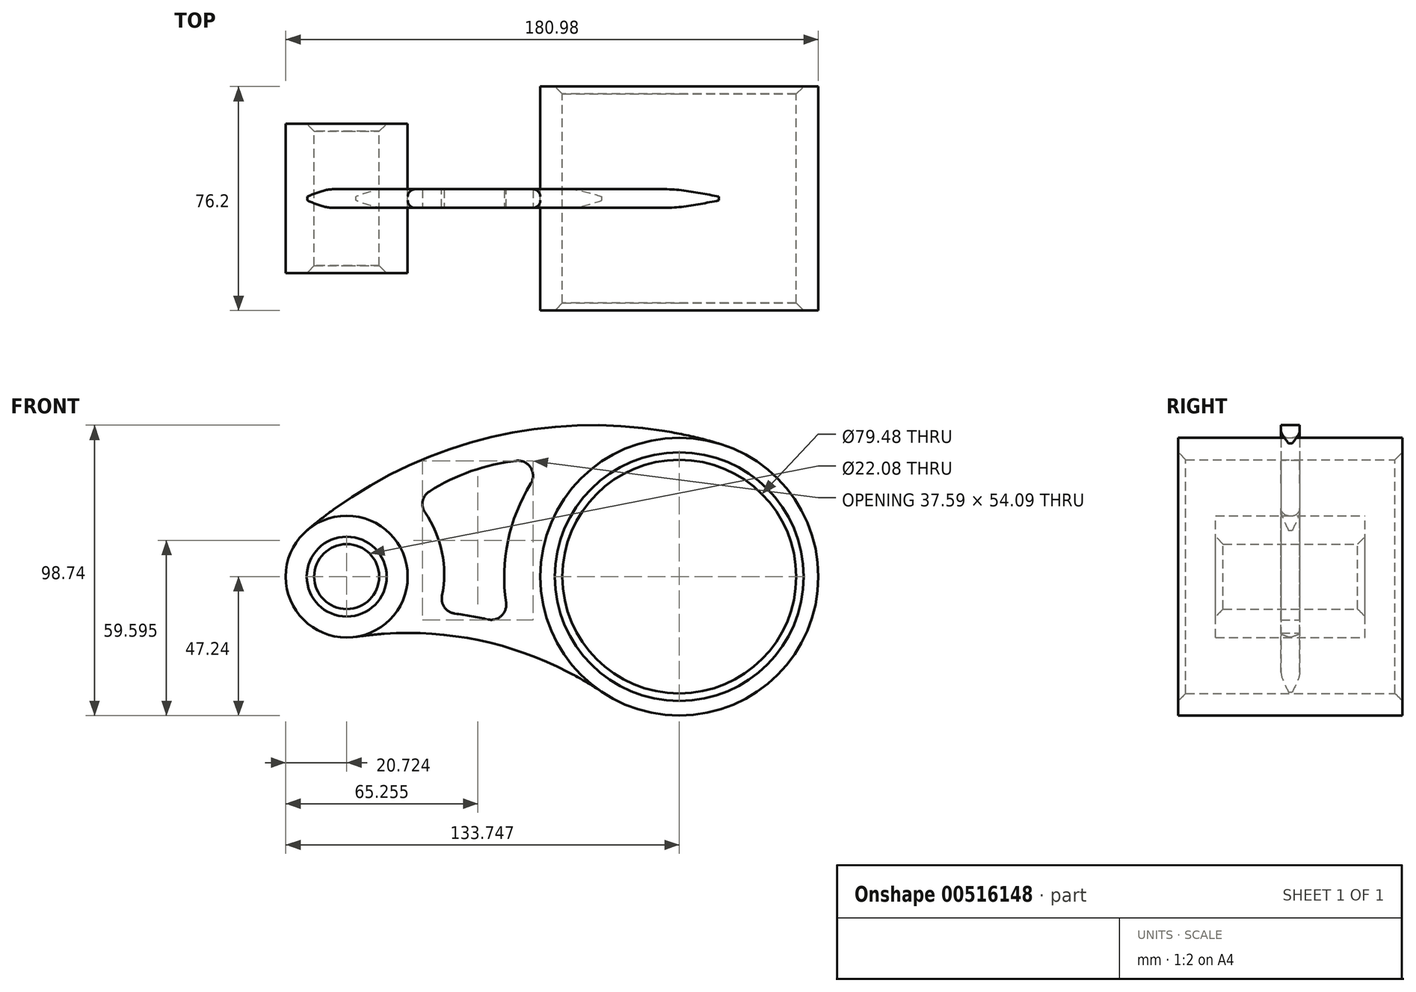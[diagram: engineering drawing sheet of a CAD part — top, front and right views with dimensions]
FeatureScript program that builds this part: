
annotation { "Feature Type Name" : "Feature", "Feature Type Description" : "" }
export const myFeature = defineFeature(function(context is Context, id is Id, definition is map)
    precondition{}
    {
        {
            var Q0;
            Q0=qCreatedBy(makeId("Front.planeOp"),FACE);
            var sketch = newSketch(context, id + "F0", { "sketchPlane" : qUnion([Q0])});
            skCircle(sketch, "E0", {"center": v(-66.18, 0) * mm, "radius": 11.04 * mm});
            skCircle(sketch, "E1", {"center": v(-66.18, 0) * mm, "radius": 20.73 * mm});
            skSolve(sketch);
        }
        {
            var Q0;
            Q0 = qSketchRegion(id + "F0", true);
            extrude(context, id + "F1", {"entities" : qUnion([Q0]), "endBound" : BoundingType.SYMMETRIC, "depth" : 50.8 * mm, "offsetDistance" : 25.4 * mm});
        }
        {
            var Q0;
            Q0=qCreatedBy(makeId("Front.planeOp"),FACE);
            var sketch = newSketch(context, id + "F2", { "sketchPlane" : qUnion([Q0])});
            skCircle(sketch, "E2", {"center": v(46.85, 0) * mm, "radius": 47.24 * mm});
            skCircle(sketch, "E3", {"center": v(46.85, 0) * mm, "radius": 39.74 * mm});
            skSolve(sketch);
        }
        {
            var Q0;
            Q0=makeQuery(id+"F2.imprint","IMPRINT",FACE,{"disambiguationData":[TD([[makeQuery(id+"F2.imprint","IMPRINT",EDGE,{"derivedFrom":sQuery(id+"F2.wireOp",EDGE,"E2")}),1.0]])]});
            extrude(context, id + "F3", {"entities" : qUnion([Q0]), "endBound" : BoundingType.SYMMETRIC, "depth" : 76.2 * mm, "offsetDistance" : 25.4 * mm});
        }
        {
            var Q0;
            Q0=qCreatedBy(makeId("Front.planeOp"),FACE);
            var sketch = newSketch(context, id + "F4", { "sketchPlane" : qUnion([Q0])});
            skArc(sketch, "E4.0", {"start": v(-63.08, -20.5) * mm, "mid": v(-47.31, 8.59) * mm, "end": v(-79.6, 15.8) * mm});
            skArc(sketch, "E5", {"start": v(60.31, 45.28) * mm, "mid": v(-13.38, 48.28) * mm, "end": v(-79.6, 15.8) * mm});
            skArc(sketch, "E6", {"start": v(20.53, -39.23) * mm, "mid": v(-19.52, -22.03) * mm, "end": v(-63.08, -20.5) * mm});
            skArc(sketch, "E7.0", {"start": v(60.31, 45.28) * mm, "mid": v(4.1, 20.12) * mm, "end": v(20.53, -39.23) * mm});
            skSolve(sketch);
        }
        {
            var Q0;
            Q0 = qSketchRegion(id + "F4", true);
            extrude(context, id + "F5", {"entities" : qUnion([Q0]), "endBound" : BoundingType.SYMMETRIC, "depth" : 6.35 * mm, "offsetDistance" : 25.4 * mm});
        }
        {
            var Q0;
            Q0=makeQuery(id+"F5.opExtrude","CAP_EDGE",EDGE,{"disambiguationData":[OSD([sQuery(id+"F4.wireOp",EDGE,"E4.0")])],"isStart":false});
            var Q1;
            Q1=makeQuery(id+"F5.opExtrude","CAP_EDGE",EDGE,{"disambiguationData":[OSD([sQuery(id+"F4.wireOp",EDGE,"E4.0")])],"isStart":true});
            var Q2;
            Q2=makeQuery(id+"F5.opExtrude","CAP_EDGE",EDGE,{"disambiguationData":[OSD([sQuery(id+"F4.wireOp",EDGE,"E7.0")])],"isStart":true});
            var Q3;
            Q3=makeQuery(id+"F5.opExtrude","CAP_EDGE",EDGE,{"disambiguationData":[OSD([sQuery(id+"F4.wireOp",EDGE,"E7.0")])],"isStart":false});
            var Q4;
            Q4=makeQuery(id+"F5.opExtrude","CAP_EDGE",EDGE,{"disambiguationData":[OSD([sQuery(id+"F4.wireOp",EDGE,"E7.0")])],"isStart":false});
            fillet(context, id + "F6", {"entities" : qUnion([Q0, Q1, Q2, Q3, Q4]), "radius" : 2.54 * mm, "tangentPropagation" : true, "allowEdgeOverflow" : false});
        }
        {
            var Q0;
            Q0=makeQuery(id+"F1.opExtrude","CAP_EDGE",EDGE,{"disambiguationData":[OSD([sQuery(id+"F0.wireOp",EDGE,"E0")])],"isStart":false});
            var Q1;
            Q1=makeQuery(id+"F3.opExtrude","CAP_EDGE",EDGE,{"disambiguationData":[OSD([sQuery(id+"F2.wireOp",EDGE,"E3")])],"isStart":false});
            var Q2;
            Q2=makeQuery(id+"F3.opExtrude","CAP_EDGE",EDGE,{"disambiguationData":[OSD([sQuery(id+"F2.wireOp",EDGE,"E3")])],"isStart":true});
            var Q3;
            Q3=makeQuery(id+"F1.opExtrude","CAP_EDGE",EDGE,{"disambiguationData":[OSD([sQuery(id+"F0.wireOp",EDGE,"E0")])],"isStart":true});
            chamfer(context, id + "F7", {"entities" : qUnion([Q0, Q1, Q2, Q3]), "width" : 2.54 * mm, "tangentPropagation" : true});
        }
        {
            var Q0;
            Q0=makeQuery(id+"F5.opExtrude","CAP_FACE",FACE,{"disambiguationData":[OSD([sQuery(id+"F4.wireOp",EDGE,"E4.0"),sQuery(id+"F4.wireOp",EDGE,"E5"),sQuery(id+"F4.wireOp",EDGE,"E6"),sQuery(id+"F4.wireOp",EDGE,"E7.0")])],"isStart":false});
            var sketch = newSketch(context, id + "F8", { "sketchPlane" : qUnion([Q0])});
            skArc(sketch, "E8", {"start": v(2.37, 39.8) * mm, "mid": v(-21.37, 36.7) * mm, "end": v(-42.7, 25.81) * mm});
            skArc(sketch, "E9", {"start": v(-35.28, -11.84) * mm, "mid": v(-33.76, 8.02) * mm, "end": v(-42.7, 25.81) * mm});
            skArc(sketch, "E10", {"start": v(2.37, 39.8) * mm, "mid": v(-11.13, 13.31) * mm, "end": v(-10.46, -16.4) * mm});
            skArc(sketch, "E11", {"start": v(-10.46, -16.4) * mm, "mid": v(-22.79, -13.65) * mm, "end": v(-35.28, -11.84) * mm});
            skSolve(sketch);
        }
        {
            var Q0;
            Q0=makeQuery(id+"F8.imprint","IMPRINT",FACE,{"disambiguationData":[TD([[makeQuery(id+"F8.imprint","IMPRINT",EDGE,{"derivedFrom":sQuery(id+"F8.wireOp",EDGE,"E8")}),1.0]])]});
            extrude(context, id + "F9", {"entities" : qUnion([Q0]), "operationType" : NewBodyOperationType.REMOVE, "endBound" : BoundingType.THROUGH_ALL, "oppositeDirection" : true, "depth" : 25.4 * mm, "offsetDistance" : 25.4 * mm});
        }
        {
            var Q0;
            Q0=makeQuery(id+"F9.boolean.opBoolean","COPY",EDGE,{"derivedFrom":makeQuery(id+"F9.opExtrude","SWEPT_EDGE",EDGE,{"disambiguationData":[OSD([sQuery(id+"F8.wireOp",EDGE,"E8"),sQuery(id+"F8.wireOp",EDGE,"E9")])]})});
            var Q1;
            Q1=makeQuery(id+"F9.boolean.opBoolean","COPY",EDGE,{"derivedFrom":makeQuery(id+"F9.opExtrude","SWEPT_EDGE",EDGE,{"disambiguationData":[OSD([sQuery(id+"F8.wireOp",EDGE,"E8"),sQuery(id+"F8.wireOp",EDGE,"E10")])]})});
            var Q2;
            Q2=makeQuery(id+"F9.boolean.opBoolean","COPY",EDGE,{"derivedFrom":makeQuery(id+"F9.opExtrude","SWEPT_EDGE",EDGE,{"disambiguationData":[OSD([sQuery(id+"F8.wireOp",EDGE,"E10"),sQuery(id+"F8.wireOp",EDGE,"E11")])]})});
            var Q3;
            Q3=makeQuery(id+"F9.boolean.opBoolean","COPY",EDGE,{"derivedFrom":makeQuery(id+"F9.opExtrude","SWEPT_EDGE",EDGE,{"disambiguationData":[OSD([sQuery(id+"F8.wireOp",EDGE,"E9"),sQuery(id+"F8.wireOp",EDGE,"E11")])]})});
            fillet(context, id + "F10", {"entities" : qUnion([Q0, Q1, Q2, Q3]), "radius" : 5.08 * mm, "tangentPropagation" : true, "allowEdgeOverflow" : false});
        }
    });
